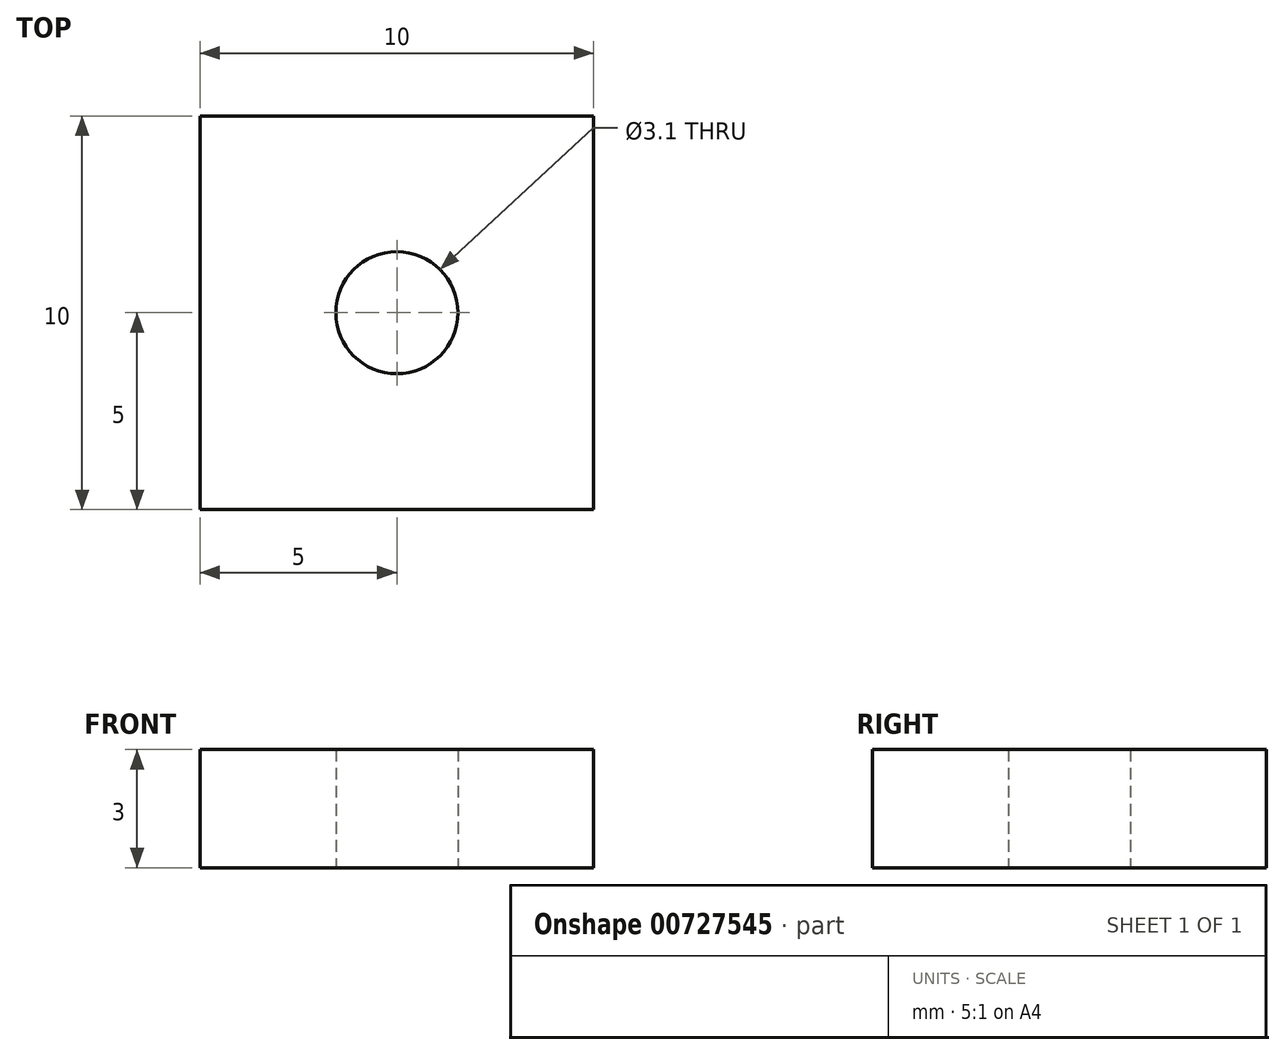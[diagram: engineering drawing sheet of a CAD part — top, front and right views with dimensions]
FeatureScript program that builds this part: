
annotation { "Feature Type Name" : "Feature", "Feature Type Description" : "" }
export const myFeature = defineFeature(function(context is Context, id is Id, definition is map)
    precondition{}
    {
        {
            var Q0;
            Q0=qCreatedBy(makeId("Top.planeOp"),FACE);
            var sketch = newSketch(context, id + "F0", { "sketchPlane" : qUnion([Q0])});
            skLineSegment(sketch, "E0.bottom", {"start": v(-5, 5) * mm, "end": v(5, 5) * mm});
            skLineSegment(sketch, "E0.top", {"start": v(-5, -5) * mm, "end": v(5, -5) * mm});
            skLineSegment(sketch, "E0.left", {"start": v(-5, 5) * mm, "end": v(-5, -5) * mm});
            skLineSegment(sketch, "E0.right", {"start": v(5, 5) * mm, "end": v(5, -5) * mm});
            skPoint(sketch, "E0.middle", {"position": v(0, 0) * mm});
            skCircle(sketch, "E1", {"center": v(0, 0) * mm, "radius": 1.55 * mm});
            skSolve(sketch);
        }
        {
            var Q0;
            Q0=makeQuery(id+"F0.imprint","IMPRINT",FACE,{"disambiguationData":[TD([[makeQuery(id+"F0.imprint","IMPRINT",EDGE,{"derivedFrom":sQuery(id+"F0.wireOp",EDGE,"E0.bottom")}),-1.0]])]});
            extrude(context, id + "F1", {"entities" : qUnion([Q0]), "depth" : 3 * mm, "offsetDistance" : 25 * mm});
        }
    });
